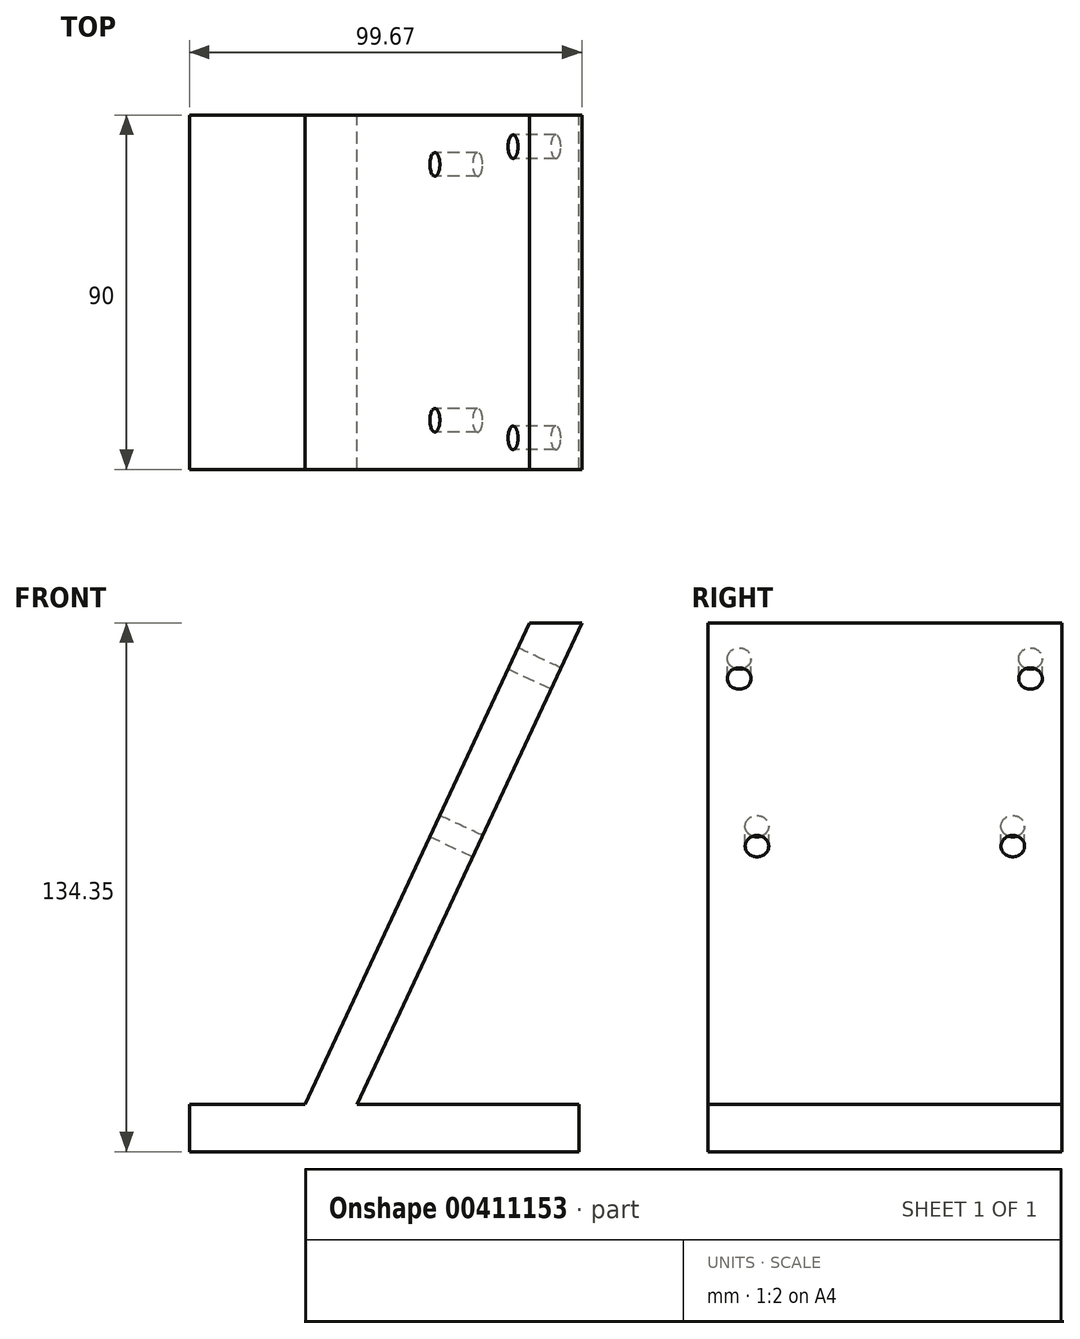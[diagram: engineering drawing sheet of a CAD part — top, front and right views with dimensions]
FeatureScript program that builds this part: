
annotation { "Feature Type Name" : "Feature", "Feature Type Description" : "" }
export const myFeature = defineFeature(function(context is Context, id is Id, definition is map)
    precondition{}
    {
        {
            var Q0;
            Q0=qCreatedBy(makeId("Front.planeOp"),FACE);
            var sketch = newSketch(context, id + "F0", { "sketchPlane" : qUnion([Q0])});
            skLineSegment(sketch, "E0.bottom", {"start": v(0, 0) * mm, "end": v(-36, 0) * mm});
            skLineSegment(sketch, "E0.top", {"start": v(0, -12) * mm, "end": v(-36, -12) * mm});
            skLineSegment(sketch, "E0.left", {"start": v(0, 0) * mm, "end": v(0, -12) * mm});
            skLineSegment(sketch, "E0.right", {"start": v(-36, 0) * mm, "end": v(-36, -12) * mm});
            skLineSegment(sketch, "E1.bottom", {"start": v(0, 0) * mm, "end": v(63, 0) * mm});
            skLineSegment(sketch, "E1.top", {"start": v(0, -12) * mm, "end": v(63, -12) * mm});
            skLineSegment(sketch, "E1.right", {"start": v(63, 0) * mm, "end": v(63, -12) * mm});
            skLineSegment(sketch, "E2", {"start": v(0, 0) * mm, "end": v(57.05, 122.35) * mm});
            skLineSegment(sketch, "E3", {"start": v(6.62, 0) * mm, "end": v(63.67, 122.35) * mm});
            skLineSegment(sketch, "E4", {"start": v(-6.62, 0) * mm, "end": v(50.43, 122.35) * mm});
            skLineSegment(sketch, "E5", {"start": v(50.43, 122.35) * mm, "end": v(63.67, 122.35) * mm});
            skSolve(sketch);
        }
        {
            var Q0;
            {var subQ0=sQuery(id+"F0.wireOp",EDGE,"E2");Q0=makeQuery(id+"F0.imprint","IMPRINT",FACE,{"disambiguationData":[TD([[makeQuery(id+"F0.imprint","IMPRINT",EDGE,{"derivedFrom":subQ0}),1.0]])]});}
            var Q1;
            {var subQ0=sQuery(id+"F0.wireOp",EDGE,"E2");Q1=makeQuery(id+"F0.imprint","IMPRINT",FACE,{"disambiguationData":[TD([[makeQuery(id+"F0.imprint","IMPRINT",EDGE,{"derivedFrom":subQ0}),-1.0]])]});}
            var Q2;
            Q2=makeQuery(id+"F0.imprint","IMPRINT",FACE,{"disambiguationData":[TD([[makeQuery(id+"F0.imprint","IMPRINT",EDGE,{"derivedFrom":sQuery(id+"F0.wireOp",EDGE,"E1.top")}),1.0]])]});
            var Q3;
            Q3=makeQuery(id+"F0.imprint","IMPRINT",FACE,{"disambiguationData":[TD([[makeQuery(id+"F0.imprint","IMPRINT",EDGE,{"derivedFrom":sQuery(id+"F0.wireOp",EDGE,"E0.top")}),-1.0]])]});
            extrude(context, id + "F1", {"entities" : qUnion([Q0, Q1, Q2, Q3]), "depth" : 90 * mm});
        }
        {
            var Q0;
            Q0=makeQuery(id+"F1.opExtrude","SWEPT_FACE",FACE,{"disambiguationData":[OSD([sQuery(id+"F0.wireOp",EDGE,"E4")])]});
            var sketch = newSketch(context, id + "F2", { "sketchPlane" : qUnion([Q0])});
            skPoint(sketch, "E6", {"position": v(82, 122.2) * mm});
            skPoint(sketch, "E7", {"position": v(8, 122.2) * mm});
            skCircle(sketch, "E8", {"center": v(8, 122.2) * mm, "radius": 3 * mm});
            skCircle(sketch, "E9", {"center": v(82, 122.2) * mm, "radius": 3 * mm});
            skSolve(sketch);
        }
        {
            var Q0;
            Q0=makeQuery(id+"F2.imprint","IMPRINT",FACE,{"disambiguationData":[TD([[makeQuery(id+"F2.imprint","IMPRINT",EDGE,{"derivedFrom":sQuery(id+"F2.wireOp",EDGE,"E8")}),1.0]])]});
            var Q1;
            Q1=makeQuery(id+"F2.imprint","IMPRINT",FACE,{"disambiguationData":[TD([[makeQuery(id+"F2.imprint","IMPRINT",EDGE,{"derivedFrom":sQuery(id+"F2.wireOp",EDGE,"E9")}),1.0]])]});
            extrude(context, id + "F3", {"entities" : qUnion([Q0, Q1]), "operationType" : NewBodyOperationType.REMOVE, "endBound" : BoundingType.THROUGH_ALL, "oppositeDirection" : true, "depth" : 25 * mm});
        }
        {
            var Q0;
            Q0=makeQuery(id+"F1.opExtrude","SWEPT_FACE",FACE,{"disambiguationData":[OSD([sQuery(id+"F0.wireOp",EDGE,"E4")])]});
            var sketch = newSketch(context, id + "F4", { "sketchPlane" : qUnion([Q0])});
            skPoint(sketch, "E10", {"position": v(12.5, 75.2) * mm});
            skPoint(sketch, "E11", {"position": v(77.5, 75.2) * mm});
            skCircle(sketch, "E12", {"center": v(12.5, 75.2) * mm, "radius": 3 * mm});
            skCircle(sketch, "E13", {"center": v(77.5, 75.2) * mm, "radius": 3 * mm});
            skSolve(sketch);
        }
        {
            var Q0;
            Q0=makeQuery(id+"F4.imprint","IMPRINT",FACE,{"disambiguationData":[TD([[makeQuery(id+"F4.imprint","IMPRINT",EDGE,{"derivedFrom":sQuery(id+"F4.wireOp",EDGE,"E12")}),1.0]])]});
            var Q1;
            Q1=makeQuery(id+"F4.imprint","IMPRINT",FACE,{"disambiguationData":[TD([[makeQuery(id+"F4.imprint","IMPRINT",EDGE,{"derivedFrom":sQuery(id+"F4.wireOp",EDGE,"E13")}),1.0]])]});
            extrude(context, id + "F5", {"entities" : qUnion([Q0, Q1]), "operationType" : NewBodyOperationType.REMOVE, "endBound" : BoundingType.THROUGH_ALL, "oppositeDirection" : true, "depth" : 25 * mm});
        }
    });
